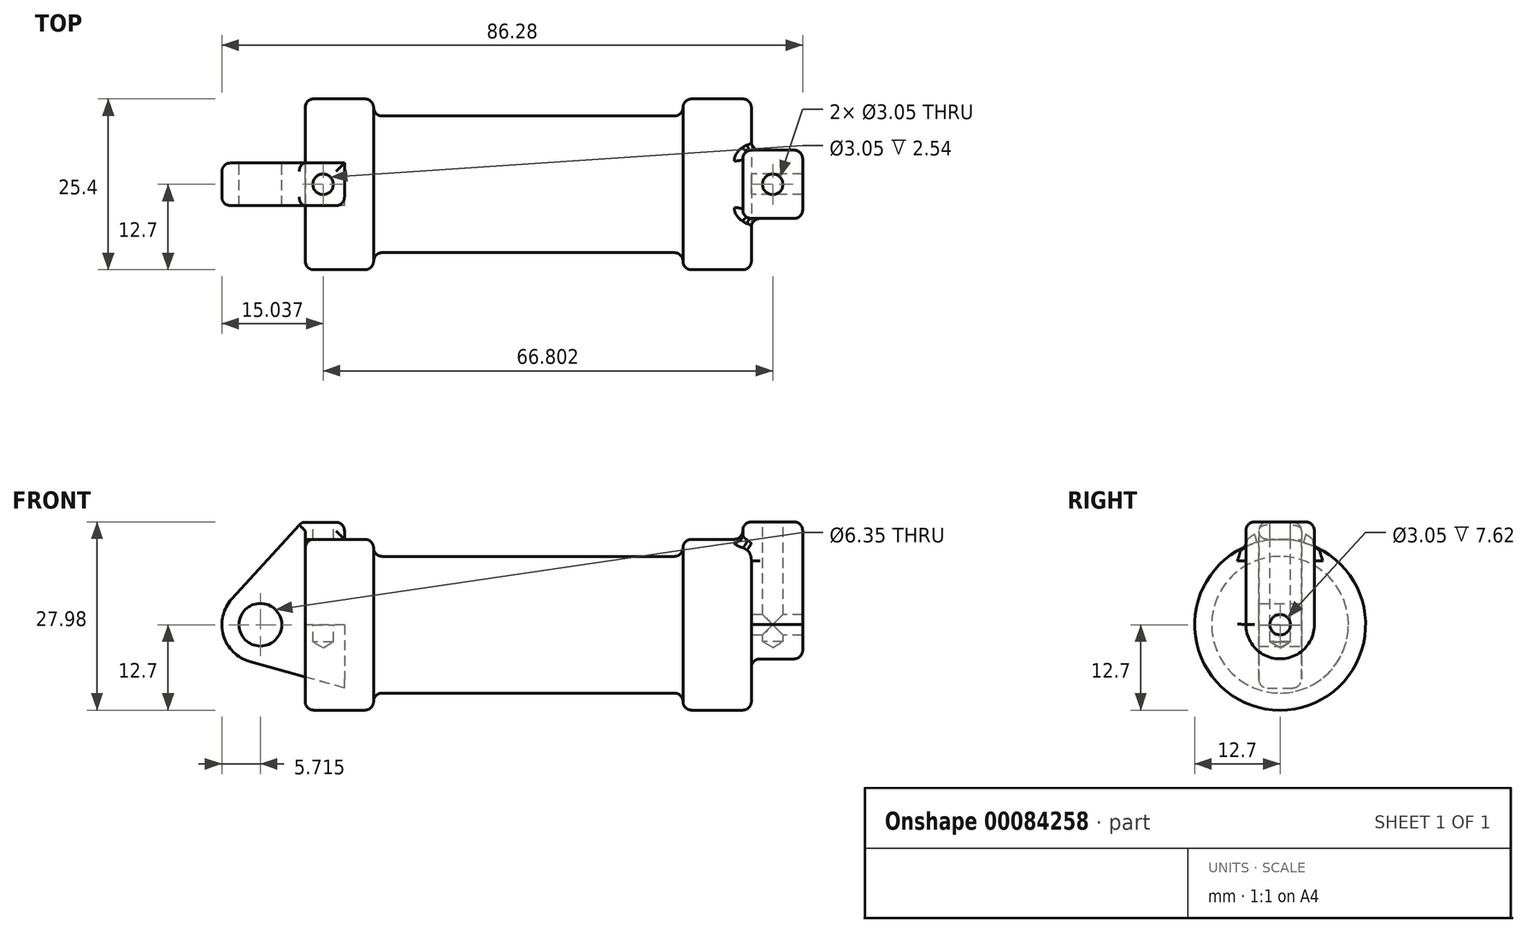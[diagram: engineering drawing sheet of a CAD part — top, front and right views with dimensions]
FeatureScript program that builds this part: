
annotation { "Feature Type Name" : "Feature", "Feature Type Description" : "" }
export const myFeature = defineFeature(function(context is Context, id is Id, definition is map)
    precondition{}
    {
        {
            var Q0;
            Q0=qCreatedBy(makeId("Front.planeOp"),FACE);
            var sketch = newSketch(context, id + "F0", { "sketchPlane" : qUnion([Q0])});
            skLineSegment(sketch, "E0", {"start": v(0, 0) * mm, "end": v(0, 12.7) * mm});
            skLineSegment(sketch, "E1", {"start": v(0, 12.7) * mm, "end": v(10.16, 12.7) * mm});
            skLineSegment(sketch, "E2", {"start": v(10.16, 12.7) * mm, "end": v(10.16, 10.16) * mm});
            skLineSegment(sketch, "E3", {"start": v(10.16, 10.16) * mm, "end": v(56.13, 10.16) * mm});
            skLineSegment(sketch, "E4", {"start": v(56.13, 10.16) * mm, "end": v(56.13, 12.7) * mm});
            skLineSegment(sketch, "E5", {"start": v(56.13, 12.7) * mm, "end": v(66.3, 12.7) * mm});
            skLineSegment(sketch, "E6", {"start": v(66.3, 12.7) * mm, "end": v(66.3, 0) * mm});
            skLineSegment(sketch, "E7", {"start": v(66.3, 0) * mm, "end": v(0, 0) * mm});
            skLineSegment(sketch, "E8", {"start": v(5.84, 15.24) * mm, "end": v(-0.5, 15.24) * mm});
            skLineSegment(sketch, "E9", {"start": v(-0.5, 15.24) * mm, "end": v(-10.88, 3.85) * mm});
            skLineSegment(sketch, "E10", {"start": v(0, 0) * mm, "end": v(-6.65, 0) * mm});
            skCircle(sketch, "E11", {"center": v(-6.65, 0) * mm, "radius": 5.72 * mm});
            skCircle(sketch, "E12", {"center": v(-6.65, 0) * mm, "radius": 3.18 * mm});
            skLineSegment(sketch, "E13", {"start": v(5.84, 15.24) * mm, "end": v(5.84, -9.4) * mm});
            skLineSegment(sketch, "E14", {"start": v(5.84, -9.4) * mm, "end": v(-8.18, -5.5) * mm});
            skSolve(sketch);
        }
        {
            var Q0;
            {var subQ0=sQuery(id+"F0.wireOp",EDGE,"E0");Q0=makeQuery(id+"F0.imprint","IMPRINT",FACE,{"disambiguationData":[TD([[makeQuery(id+"F0.imprint","IMPRINT",EDGE,{"derivedFrom":subQ0}),-1.0]])]});}
            var Q1;
            {var subQ0=sQuery(id+"F0.wireOp",EDGE,"E2");Q1=makeQuery(id+"F0.imprint","IMPRINT",FACE,{"disambiguationData":[TD([[makeQuery(id+"F0.imprint","IMPRINT",EDGE,{"derivedFrom":subQ0}),-1.0]])]});}
            var Q2;
            Q2=sQuery(id+"F0.wireOp",EDGE,"E7");
            revolve(context, id + "F1", {"entities" : qUnion([Q0, Q1]), "axis" : qUnion([Q2]), "revolveType" : RevolveType.FULL});
        }
        {
            var Q0;
            {var subQ3=sQuery(id+"F0.wireOp",EDGE,"E0");Q0=makeQuery(id+"F0.imprint","IMPRINT",FACE,{"disambiguationData":[TD([[makeQuery(id+"F0.imprint","IMPRINT",EDGE,{"derivedFrom":subQ3}),1.0]])]});}
            var Q1;
            {var subQ4=sQuery(id+"F0.wireOp",EDGE,"E12");Q1=makeQuery(id+"F0.imprint","IMPRINT",FACE,{"disambiguationData":[TD([[makeQuery(id+"F0.imprint","IMPRINT",EDGE,{"derivedFrom":subQ4}),-1.0]])]});}
            var Q2;
            {var subQ0=sQuery(id+"F0.wireOp",EDGE,"E14");Q2=makeQuery(id+"F0.imprint","IMPRINT",FACE,{"disambiguationData":[TD([[makeQuery(id+"F0.imprint","IMPRINT",EDGE,{"derivedFrom":subQ0}),-1.0]])]});}
            extrude(context, id + "F2", {"entities" : qUnion([Q0, Q1, Q2]), "endBound" : BoundingType.SYMMETRIC, "depth" : 6.35 * mm});
        }
        {
            var Q0;
            Q0=makeQuery(id+"F1.opRevolve","SWEPT_FACE",FACE,{"disambiguationData":[OSD([sQuery(id+"F0.wireOp",EDGE,"E6")])]});
            var sketch = newSketch(context, id + "F3", { "sketchPlane" : qUnion([Q0])});
            skCircle(sketch, "E15", {"center": v(0, 0) * mm, "radius": 5.08 * mm});
            skCircle(sketch, "E16", {"center": v(0, 0) * mm, "radius": 1.52 * mm});
            skLineSegment(sketch, "E17", {"start": v(-5.08, 0.06) * mm, "end": v(-5.08, 15.28) * mm});
            skLineSegment(sketch, "E18", {"start": v(-5.08, 15.28) * mm, "end": v(5.08, 15.28) * mm});
            skLineSegment(sketch, "E19", {"start": v(5.08, 15.28) * mm, "end": v(5.08, 0.04) * mm});
            skSolve(sketch);
        }
        {
            var Q0;
            {var subQ0=sQuery(id+"F3.wireOp",EDGE,"E17");var subQ1=sQuery(id+"F3.wireOp",EDGE,"E15");var subQ2=makeQuery(id+"F3.imprint","INTERSECT",VERTEX,{"derivedFrom":[subQ1,subQ0]});Q0=makeQuery(id+"F3.imprint","IMPRINT",FACE,{"disambiguationData":[TD([[makeQuery(id+"F3.imprint","IMPRINT",EDGE,{"disambiguationData":[TD([[subQ2,1.0]])],"derivedFrom":subQ1}),-1.0]])]});}
            var Q1;
            {var subQ0=sQuery(id+"F3.wireOp",EDGE,"E18");Q1=makeQuery(id+"F3.imprint","IMPRINT",FACE,{"disambiguationData":[TD([[makeQuery(id+"F3.imprint","IMPRINT",EDGE,{"derivedFrom":subQ0}),-1.0]])]});}
            var Q2;
            Q2=makeQuery(id+"F3.imprint","IMPRINT",FACE,{"disambiguationData":[TD([[makeQuery(id+"F3.imprint","IMPRINT",EDGE,{"derivedFrom":sQuery(id+"F3.wireOp",EDGE,"E16")}),-1.0]])]});
            extrude(context, id + "F4", {"entities" : qUnion([Q0, Q1, Q2]), "operationType" : NewBodyOperationType.ADD, "depth" : 7.62 * mm, "hasSecondDirection" : true, "secondDirectionOppositeDirection" : true, "secondDirectionDepth" : 1.27 * mm});
        }
        {
            var Q0;
            Q0=makeQuery(id+"F2.opExtrude","SWEPT_FACE",FACE,{"disambiguationData":[OSD([sQuery(id+"F0.wireOp",EDGE,"E8")])]});
            var sketch = newSketch(context, id + "F5", { "sketchPlane" : qUnion([Q0])});
            skLineSegment(sketch, "E20", {"start": v(-0.5, 3.18) * mm, "end": v(5.84, -3.18) * mm, "construction": true});
            skLineSegment(sketch, "E21", {"start": v(5.84, 3.18) * mm, "end": v(-0.5, -3.18) * mm, "construction": true});
            skCircle(sketch, "E22", {"center": v(2.67, 0) * mm, "radius": 1.52 * mm, "construction": true});
            skSolve(sketch);
        }
        {
            var Q0;
            Q0=sQuery(id+"F5.wireOp",VERTEX,"E22.center");
            var Q1;
            Q1=makeQuery(id+"F2.opExtrude","SWEPT_BODY",BODY,{"disambiguationData":[OSD([sQuery(id+"F0.wireOp",EDGE,"E0"),sQuery(id+"F0.wireOp",EDGE,"E1"),sQuery(id+"F0.wireOp",EDGE,"E7"),sQuery(id+"F0.wireOp",EDGE,"E8"),sQuery(id+"F0.wireOp",EDGE,"E9"),sQuery(id+"F0.wireOp",EDGE,"E11"),sQuery(id+"F0.wireOp",EDGE,"E12"),sQuery(id+"F0.wireOp",EDGE,"E13"),sQuery(id+"F0.wireOp",EDGE,"E14")])]});
            hole(context, id + "F6", {"style" : HoleStyle.SIMPLE, "endStyle" : HoleEndStyle.BLIND, "holeDiameter" : 3.05 * mm, "holeDepth" : 17.78 * mm, "locations" : qUnion([Q0]), "scope" : qUnion([Q1])});
        }
        {
            var Q0;
            Q0=makeQuery(id+"F4.opExtrude","SWEPT_FACE",FACE,{"disambiguationData":[OSD([sQuery(id+"F3.wireOp",EDGE,"E18")])]});
            var sketch = newSketch(context, id + "F7", { "sketchPlane" : qUnion([Q0])});
            skLineSegment(sketch, "E23", {"start": v(65.02, 5.08) * mm, "end": v(73.91, -5.08) * mm, "construction": true});
            skLineSegment(sketch, "E24", {"start": v(73.91, 5.08) * mm, "end": v(65.02, -5.08) * mm, "construction": true});
            skCircle(sketch, "E25", {"center": v(69.47, 0) * mm, "radius": 1.52 * mm});
            skSolve(sketch);
        }
        {
            var Q0;
            Q0=sQuery(id+"F7.wireOp",VERTEX,"E25.center");
            var Q1;
            Q1=makeQuery(id+"F1.opRevolve","SWEPT_BODY",BODY,{"disambiguationData":[OSD([sQuery(id+"F0.wireOp",EDGE,"E0"),sQuery(id+"F0.wireOp",EDGE,"E1"),sQuery(id+"F0.wireOp",EDGE,"E2"),sQuery(id+"F0.wireOp",EDGE,"E3"),sQuery(id+"F0.wireOp",EDGE,"E4"),sQuery(id+"F0.wireOp",EDGE,"E5"),sQuery(id+"F0.wireOp",EDGE,"E6"),sQuery(id+"F0.wireOp",EDGE,"E7")])]});
            hole(context, id + "F8", {"style" : HoleStyle.SIMPLE, "endStyle" : HoleEndStyle.BLIND, "holeDiameter" : 3.05 * mm, "holeDepth" : 17.78 * mm, "locations" : qUnion([Q0]), "scope" : qUnion([Q1])});
        }
        {
            var Q0;
            Q0=makeQuery(id+"F1.opRevolve","SWEPT_EDGE",EDGE,{"disambiguationData":[OSD([sQuery(id+"F0.wireOp",EDGE,"E0"),sQuery(id+"F0.wireOp",EDGE,"E1")])]});
            var Q1;
            Q1=makeQuery(id+"F1.opRevolve","SWEPT_EDGE",EDGE,{"disambiguationData":[OSD([sQuery(id+"F0.wireOp",EDGE,"E1"),sQuery(id+"F0.wireOp",EDGE,"E2")])]});
            var Q2;
            Q2=makeQuery(id+"F1.opRevolve","SWEPT_FACE",FACE,{"disambiguationData":[OSD([sQuery(id+"F0.wireOp",EDGE,"E1")])]});
            var Q3;
            Q3=makeQuery(id+"F1.opRevolve","SWEPT_EDGE",EDGE,{"disambiguationData":[OSD([sQuery(id+"F0.wireOp",EDGE,"E2"),sQuery(id+"F0.wireOp",EDGE,"E3")])]});
            var Q4;
            Q4=makeQuery(id+"F1.opRevolve","SWEPT_EDGE",EDGE,{"disambiguationData":[OSD([sQuery(id+"F0.wireOp",EDGE,"E4"),sQuery(id+"F0.wireOp",EDGE,"E5")])]});
            var Q5;
            Q5=makeQuery(id+"F1.opRevolve","SWEPT_EDGE",EDGE,{"disambiguationData":[OSD([sQuery(id+"F0.wireOp",EDGE,"E5"),sQuery(id+"F0.wireOp",EDGE,"E6")])]});
            var Q6;
            Q6=makeQuery(id+"F1.opRevolve","SWEPT_EDGE",EDGE,{"disambiguationData":[OSD([sQuery(id+"F0.wireOp",EDGE,"E3"),sQuery(id+"F0.wireOp",EDGE,"E4")])]});
            fillet(context, id + "F9", {"entities" : qUnion([Q0, Q1, Q2, Q3, Q4, Q5, Q6]), "radius" : 1.27 * mm, "tangentPropagation" : true, "allowEdgeOverflow" : false});
        }
        {
            var Q0;
            Q0=makeQuery(id+"F4.opExtrude","CAP_EDGE",EDGE,{"disambiguationData":[OSD([sQuery(id+"F3.wireOp",EDGE,"E17")])],"isStart":false});
            var Q1;
            Q1=makeQuery(id+"F4.opExtrude","CAP_EDGE",EDGE,{"disambiguationData":[OSD([sQuery(id+"F3.wireOp",EDGE,"E15")])],"isStart":false});
            var Q2;
            Q2=makeQuery(id+"F4.boolean.opBoolean","INTERSECT",EDGE,{"derivedFrom":[makeQuery(id+"F1.opRevolve","SWEPT_FACE",FACE,{"disambiguationData":[OSD([sQuery(id+"F0.wireOp",EDGE,"E6")])]}),makeQuery(id+"F4.opExtrude","SWEPT_FACE",FACE,{"disambiguationData":[OSD([sQuery(id+"F3.wireOp",EDGE,"E15")])]})]});
            var Q3;
            Q3=makeQuery(id+"F4.boolean.opBoolean","INTERSECT",EDGE,{"derivedFrom":[makeQuery(id+"F1.opRevolve","SWEPT_FACE",FACE,{"disambiguationData":[OSD([sQuery(id+"F0.wireOp",EDGE,"E6")])]}),makeQuery(id+"F4.opExtrude","SWEPT_FACE",FACE,{"disambiguationData":[OSD([sQuery(id+"F3.wireOp",EDGE,"E17")])]})]});
            var Q4;
            Q4=makeQuery(id+"F4.boolean.opBoolean","INTERSECT",EDGE,{"derivedFrom":[makeQuery(id+"F1.opRevolve","SWEPT_FACE",FACE,{"disambiguationData":[OSD([sQuery(id+"F0.wireOp",EDGE,"E6")])]}),makeQuery(id+"F4.opExtrude","SWEPT_FACE",FACE,{"disambiguationData":[OSD([sQuery(id+"F3.wireOp",EDGE,"E19")])]})]});
            var Q5;
            Q5=makeQuery(id+"F4.boolean.opBoolean","INTERSECT",EDGE,{"derivedFrom":[makeQuery(id+"F1.opRevolve","SWEPT_FACE",FACE,{"disambiguationData":[OSD([sQuery(id+"F0.wireOp",EDGE,"E5")])]}),makeQuery(id+"F4.opExtrude","CAP_FACE",FACE,{"disambiguationData":[OSD([sQuery(id+"F3.wireOp",EDGE,"E15"),sQuery(id+"F3.wireOp",EDGE,"E16"),sQuery(id+"F3.wireOp",EDGE,"E17"),sQuery(id+"F3.wireOp",EDGE,"E18"),sQuery(id+"F3.wireOp",EDGE,"E19")])],"isStart":true})]});
            var Q6;
            Q6=makeQuery(id+"F4.opExtrude","CAP_EDGE",EDGE,{"disambiguationData":[OSD([sQuery(id+"F3.wireOp",EDGE,"E19")])],"isStart":true});
            var Q7;
            Q7=makeQuery(id+"F4.opExtrude","CAP_EDGE",EDGE,{"disambiguationData":[OSD([sQuery(id+"F3.wireOp",EDGE,"E17")])],"isStart":true});
            var Q8;
            Q8=makeQuery(id+"F4.opExtrude","SWEPT_EDGE",EDGE,{"disambiguationData":[OSD([sQuery(id+"F3.wireOp",EDGE,"E18"),sQuery(id+"F3.wireOp",EDGE,"E19")])]});
            var Q9;
            Q9=makeQuery(id+"F4.opExtrude","CAP_EDGE",EDGE,{"disambiguationData":[OSD([sQuery(id+"F3.wireOp",EDGE,"E18")])],"isStart":true});
            var Q10;
            Q10=makeQuery(id+"F4.opExtrude","CAP_EDGE",EDGE,{"disambiguationData":[OSD([sQuery(id+"F3.wireOp",EDGE,"E19")])],"isStart":false});
            var Q11;
            Q11=makeQuery(id+"F9.opFillet","BLEND_EDGE",EDGE,{"blendedFrom":[makeQuery(id+"F1.opRevolve","SWEPT_EDGE",EDGE,{"disambiguationData":[OSD([sQuery(id+"F0.wireOp",EDGE,"E5"),sQuery(id+"F0.wireOp",EDGE,"E6")])]}),makeQuery(id+"F4.opExtrude","SWEPT_FACE",FACE,{"disambiguationData":[OSD([sQuery(id+"F3.wireOp",EDGE,"E19")])]})],"blendedInto":[makeQuery(id+"F4.opExtrude","SWEPT_FACE",FACE,{"disambiguationData":[OSD([sQuery(id+"F3.wireOp",EDGE,"E19")])]})]});
            var Q12;
            Q12=makeQuery(id+"F4.opExtrude","CAP_EDGE",EDGE,{"disambiguationData":[OSD([sQuery(id+"F3.wireOp",EDGE,"E18")])],"isStart":false});
            var Q13;
            Q13=makeQuery(id+"F4.opExtrude","SWEPT_EDGE",EDGE,{"disambiguationData":[OSD([sQuery(id+"F3.wireOp",EDGE,"E17"),sQuery(id+"F3.wireOp",EDGE,"E18")])]});
            var Q14;
            Q14=makeQuery(id+"F9.opFillet","BLEND_EDGE",EDGE,{"blendedFrom":[makeQuery(id+"F1.opRevolve","SWEPT_EDGE",EDGE,{"disambiguationData":[OSD([sQuery(id+"F0.wireOp",EDGE,"E5"),sQuery(id+"F0.wireOp",EDGE,"E6")])]}),makeQuery(id+"F4.opExtrude","SWEPT_FACE",FACE,{"disambiguationData":[OSD([sQuery(id+"F3.wireOp",EDGE,"E17")])]})],"blendedInto":[makeQuery(id+"F4.opExtrude","SWEPT_FACE",FACE,{"disambiguationData":[OSD([sQuery(id+"F3.wireOp",EDGE,"E17")])]})]});
            fillet(context, id + "F10", {"entities" : qUnion([Q0, Q1, Q2, Q3, Q4, Q5, Q6, Q7, Q8, Q9, Q10, Q11, Q12, Q13, Q14]), "radius" : 1.27 * mm, "tangentPropagation" : true, "allowEdgeOverflow" : false});
        }
        {
            var Q0;
            Q0=makeQuery(id+"F2.opExtrude","CAP_EDGE",EDGE,{"disambiguationData":[OSD([sQuery(id+"F0.wireOp",EDGE,"E9")])],"isStart":false});
            var Q1;
            Q1=makeQuery(id+"F2.opExtrude","SWEPT_EDGE",EDGE,{"disambiguationData":[OSD([sQuery(id+"F0.wireOp",EDGE,"E9"),sQuery(id+"F0.wireOp",EDGE,"E11")])]});
            var Q2;
            Q2=makeQuery(id+"F2.opExtrude","CAP_EDGE",EDGE,{"disambiguationData":[OSD([sQuery(id+"F0.wireOp",EDGE,"E11")])],"isStart":true});
            var Q3;
            Q3=makeQuery(id+"F2.opExtrude","CAP_EDGE",EDGE,{"disambiguationData":[OSD([sQuery(id+"F0.wireOp",EDGE,"E9")])],"isStart":true});
            var Q4;
            Q4=makeQuery(id+"F2.opExtrude","CAP_EDGE",EDGE,{"disambiguationData":[OSD([sQuery(id+"F0.wireOp",EDGE,"E14")])],"isStart":true});
            var Q5;
            Q5=makeQuery(id+"F2.opExtrude","CAP_EDGE",EDGE,{"disambiguationData":[OSD([sQuery(id+"F0.wireOp",EDGE,"E14")])],"isStart":false});
            var Q6;
            {var subQ0=sQuery(id+"F0.wireOp",EDGE,"E0");Q6=makeQuery(id+"F9.opFillet","BLEND_EDGE",EDGE,{"blendedFrom":[makeQuery(id+"F1.opRevolve","SWEPT_EDGE",EDGE,{"disambiguationData":[OSD([subQ0,sQuery(id+"F0.wireOp",EDGE,"E1")])]}),makeQuery(id+"F1.opRevolve","SWEPT_FACE",FACE,{"disambiguationData":[OSD([subQ0])]})],"blendedInto":[makeQuery(id+"F1.opRevolve","SWEPT_FACE",FACE,{"disambiguationData":[OSD([subQ0])]})]});}
            var Q7;
            Q7=makeQuery(id+"F2.opExtrude","CAP_EDGE",EDGE,{"disambiguationData":[OSD([sQuery(id+"F0.wireOp",EDGE,"E11")])],"isStart":false});
            fillet(context, id + "F11", {"entities" : qUnion([Q0, Q1, Q2, Q3, Q4, Q5, Q6, Q7]), "radius" : 1.27 * mm, "tangentPropagation" : true, "allowEdgeOverflow" : false});
        }
        {
            var Q0;
            Q0=makeQuery(id+"F2.opExtrude","CAP_EDGE",EDGE,{"disambiguationData":[OSD([sQuery(id+"F0.wireOp",EDGE,"E8")])],"isStart":false});
            var Q1;
            Q1=makeQuery(id+"F2.opExtrude","CAP_EDGE",EDGE,{"disambiguationData":[OSD([sQuery(id+"F0.wireOp",EDGE,"E8")])],"isStart":true});
            var Q2;
            Q2=makeQuery(id+"F11.opFillet","BLEND_EDGE",EDGE,{"blendedFrom":[makeQuery(id+"F2.opExtrude","CAP_EDGE",EDGE,{"disambiguationData":[OSD([sQuery(id+"F0.wireOp",EDGE,"E9")])],"isStart":true}),makeQuery(id+"F2.opExtrude","SWEPT_FACE",FACE,{"disambiguationData":[OSD([sQuery(id+"F0.wireOp",EDGE,"E8")])]})],"blendedInto":[makeQuery(id+"F2.opExtrude","SWEPT_FACE",FACE,{"disambiguationData":[OSD([sQuery(id+"F0.wireOp",EDGE,"E8")])]})]});
            var Q3;
            Q3=makeQuery(id+"F2.opExtrude","SWEPT_EDGE",EDGE,{"disambiguationData":[OSD([sQuery(id+"F0.wireOp",EDGE,"E8"),sQuery(id+"F0.wireOp",EDGE,"E13")])]});
            var Q4;
            {var subQ0=sQuery(id+"F0.wireOp",EDGE,"E13");Q4=makeQuery(id+"F2.opExtrude","CAP_EDGE",EDGE,{"disambiguationData":[OSD([subQ0]),TDD([makeQuery(id+"F0.imprint","IMPRINT",EDGE,{"disambiguationData":[TD([[makeQuery(id+"F0.imprint","INTERSECT",VERTEX,{"derivedFrom":[sQuery(id+"F0.wireOp",EDGE,"E8"),subQ0]}),-1.0]])],"derivedFrom":subQ0})])],"isStart":false});}
            var Q5;
            Q5=makeQuery(id+"F2.opExtrude","CAP_EDGE",EDGE,{"disambiguationData":[OSD([sQuery(id+"F0.wireOp",EDGE,"E1")])],"isStart":false});
            var Q6;
            Q6=makeQuery(id+"F11.opFillet","BLEND_EDGE",EDGE,{"blendedFrom":[makeQuery(id+"F2.opExtrude","CAP_EDGE",EDGE,{"disambiguationData":[OSD([sQuery(id+"F0.wireOp",EDGE,"E9")])],"isStart":false}),makeQuery(id+"F2.opExtrude","SWEPT_FACE",FACE,{"disambiguationData":[OSD([sQuery(id+"F0.wireOp",EDGE,"E8")])]})],"blendedInto":[makeQuery(id+"F2.opExtrude","SWEPT_FACE",FACE,{"disambiguationData":[OSD([sQuery(id+"F0.wireOp",EDGE,"E8")])]})]});
            var Q7;
            Q7=makeQuery(id+"F2.opExtrude","SWEPT_EDGE",EDGE,{"disambiguationData":[OSD([sQuery(id+"F0.wireOp",EDGE,"E8"),sQuery(id+"F0.wireOp",EDGE,"E9")])]});
            fillet(context, id + "F12", {"entities" : qUnion([Q0, Q1, Q2, Q3, Q4, Q5, Q6, Q7]), "radius" : 1.27 * mm, "tangentPropagation" : true, "allowEdgeOverflow" : false});
        }
    });
